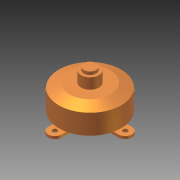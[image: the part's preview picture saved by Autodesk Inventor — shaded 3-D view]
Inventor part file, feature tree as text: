
AUTODESK INVENTOR PART (.ipt)
format: ipt  version: 2011 SP1 (Build 150282100, 282)  size: 149,504 bytes
history: native  units: in
note: dims shown in document units (in); Inventor stores cm internally (conversion verified against a paired STEP export)
features: sketch x2, revolve x1, extrude x1
ambient origin geometry x8: Origin, YZ Plane, XZ Plane, XY Plane, X Axis, Y Axis, Z Axis, Center Point
bodies: Solid1 (feature_tree)
feature tree (4):
  revolve  "Revolution1"  [1 undecoded]
  extrude  "Extrusion1"  Depth=0.544in
  sketch  "Sketch1"  dims[d0=0.424in d1=0.348in]
  sketch  "Sketch2"  dims[d2=0.183in d3=0.544in d4=0.664in d5=0.053in d6=0.107in d7=0.1565in d8=90.0deg d9=0.125in d10=0.234in d11=0.117in d12=0.234in d13=0.616in d14=0.616in d15=0.616in d16=0.084in d17=0.046in d18=0.0in]
note: 1 required parameter value undecoded (feature->parameter linkage not recoverable at this tier; creation-order binding heuristic only, values carry confidence <= 0.55)
